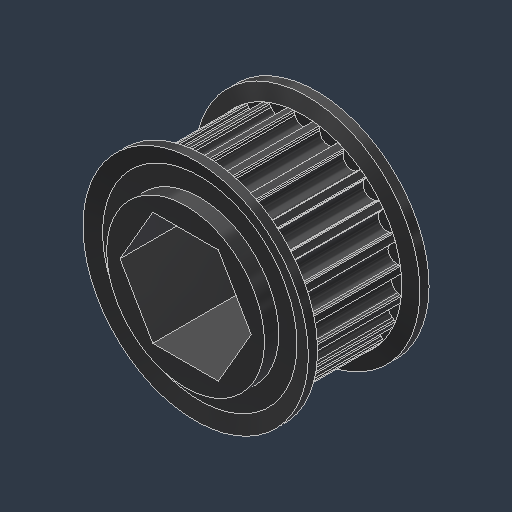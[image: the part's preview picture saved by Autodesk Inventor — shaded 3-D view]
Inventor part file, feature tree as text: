
AUTODESK INVENTOR PART (.ipt)
format: ipt  version: 2024.3 (Build 283343000, 343)  size: 286,208 bytes
history: native  units: mm (DEFAULTED — no unit token found)
features: mirror x1
ambient origin geometry x8: Origin, YZ Plane, XZ Plane, XY Plane, X Axis, Y Axis, Z Axis, Center Point
bodies: Solid1 (feature_tree)
feature tree (1):
  mirror  "Mirror1"
